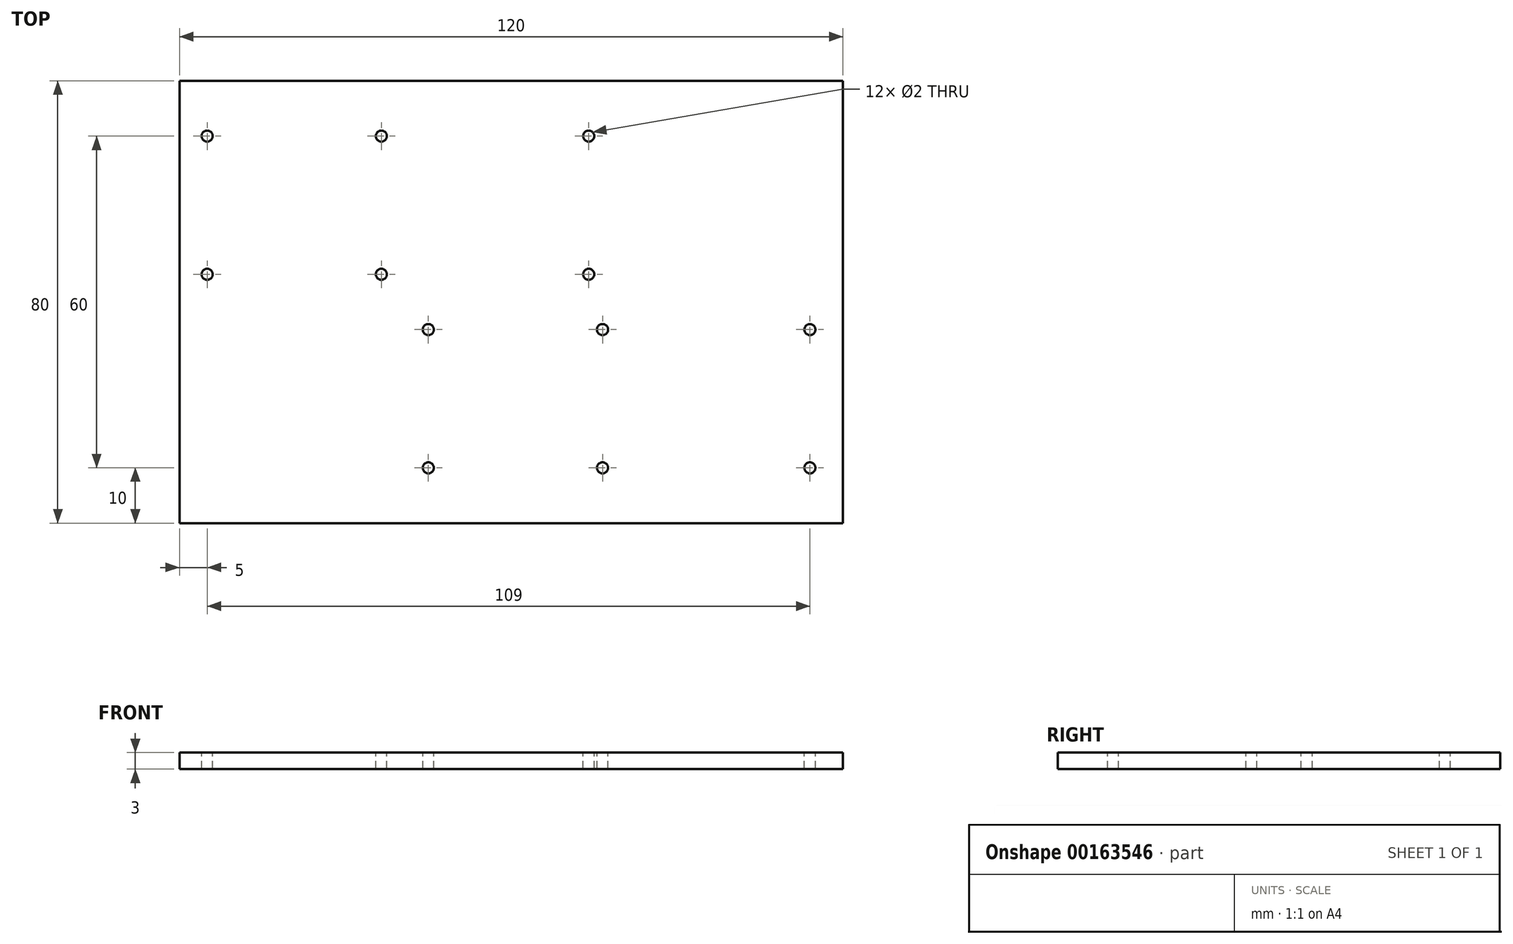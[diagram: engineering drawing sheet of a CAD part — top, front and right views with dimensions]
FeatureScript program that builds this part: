
annotation { "Feature Type Name" : "Feature", "Feature Type Description" : "" }
export const myFeature = defineFeature(function(context is Context, id is Id, definition is map)
    precondition{}
    {
        {
            var Q0;
            Q0=qCreatedBy(makeId("Top.planeOp"),FACE);
            var sketch = newSketch(context, id + "F0", { "sketchPlane" : qUnion([Q0])});
            skLineSegment(sketch, "E0.bottom", {"start": v(0, 0) * mm, "end": v(120, 0) * mm});
            skLineSegment(sketch, "E0.top", {"start": v(0, 80) * mm, "end": v(120, 80) * mm});
            skLineSegment(sketch, "E0.left", {"start": v(0, 0) * mm, "end": v(0, 80) * mm});
            skLineSegment(sketch, "E0.right", {"start": v(120, 0) * mm, "end": v(120, 80) * mm});
            skSolve(sketch);
        }
        {
            var Q0;
            Q0=makeQuery(id+"F0.imprint","IMPRINT",FACE,{"disambiguationData":[TD([[makeQuery(id+"F0.imprint","IMPRINT",EDGE,{"derivedFrom":sQuery(id+"F0.wireOp",EDGE,"E0.bottom")}),1.0]])]});
            extrude(context, id + "F1", {"entities" : qUnion([Q0]), "oppositeDirection" : true, "depth" : 3 * mm});
        }
        {
            var Q0;
            Q0=makeQuery(id+"F1.opExtrude","CAP_FACE",FACE,{"disambiguationData":[OSD([sQuery(id+"F0.wireOp",EDGE,"E0.bottom"),sQuery(id+"F0.wireOp",EDGE,"E0.top"),sQuery(id+"F0.wireOp",EDGE,"E0.left"),sQuery(id+"F0.wireOp",EDGE,"E0.right")])],"isStart":true});
            var sketch = newSketch(context, id + "F2", { "sketchPlane" : qUnion([Q0])});
            skPoint(sketch, "E1", {"position": v(5, 70) * mm});
            skPoint(sketch, "E2", {"position": v(36.5, 70) * mm});
            skPoint(sketch, "E3", {"position": v(74, 70) * mm});
            skPoint(sketch, "E4", {"position": v(5, 45) * mm});
            skPoint(sketch, "E5", {"position": v(36.5, 45) * mm});
            skPoint(sketch, "E6", {"position": v(74, 45) * mm});
            skPoint(sketch, "E7.1.0.0", {"position": v(114, 35) * mm});
            skPoint(sketch, "E7.1.0.1", {"position": v(76.5, 35) * mm});
            skPoint(sketch, "E7.1.0.2", {"position": v(45, 10) * mm});
            skPoint(sketch, "E7.1.0.3", {"position": v(76.5, 10) * mm});
            skPoint(sketch, "E7.1.0.4", {"position": v(45, 35) * mm});
            skPoint(sketch, "E7.1.0.5", {"position": v(114, 10) * mm});
            skLineSegment(sketch, "E7.direction1", {"start": v(5, 45) * mm, "end": v(45, 10) * mm, "construction": true});
            skSolve(sketch);
        }
        {
            var Q0;
            Q0=sQuery(id+"F2.wireOp",VERTEX,"E1");
            var Q1;
            Q1=sQuery(id+"F2.wireOp",VERTEX,"E7.1.0.1");
            var Q2;
            Q2=sQuery(id+"F2.wireOp",VERTEX,"E7.1.0.5");
            var Q3;
            Q3=sQuery(id+"F2.wireOp",VERTEX,"E7.1.0.0");
            var Q4;
            Q4=sQuery(id+"F2.wireOp",VERTEX,"E7.1.0.3");
            var Q5;
            Q5=sQuery(id+"F2.wireOp",VERTEX,"E6");
            var Q6;
            Q6=sQuery(id+"F2.wireOp",VERTEX,"E7.1.0.2");
            var Q7;
            Q7=sQuery(id+"F2.wireOp",VERTEX,"E7.1.0.4");
            var Q8;
            Q8=sQuery(id+"F2.wireOp",VERTEX,"E2");
            var Q9;
            Q9=sQuery(id+"F2.wireOp",VERTEX,"E3");
            var Q10;
            Q10=sQuery(id+"F2.wireOp",VERTEX,"E4");
            var Q11;
            Q11=sQuery(id+"F2.wireOp",VERTEX,"E5");
            var Q12;
            Q12=makeQuery(id+"F1.opExtrude","SWEPT_BODY",BODY,{"disambiguationData":[OSD([sQuery(id+"F0.wireOp",EDGE,"E0.bottom"),sQuery(id+"F0.wireOp",EDGE,"E0.top"),sQuery(id+"F0.wireOp",EDGE,"E0.left"),sQuery(id+"F0.wireOp",EDGE,"E0.right")])]});
            hole(context, id + "F3", {"style" : HoleStyle.SIMPLE, "endStyle" : HoleEndStyle.THROUGH, "holeDiameter" : 2 * mm, "locations" : qUnion([Q0, Q1, Q2, Q3, Q4, Q5, Q6, Q7, Q8, Q9, Q10, Q11]), "scope" : qUnion([Q12]), "isTappedThrough" : true});
        }
    });
